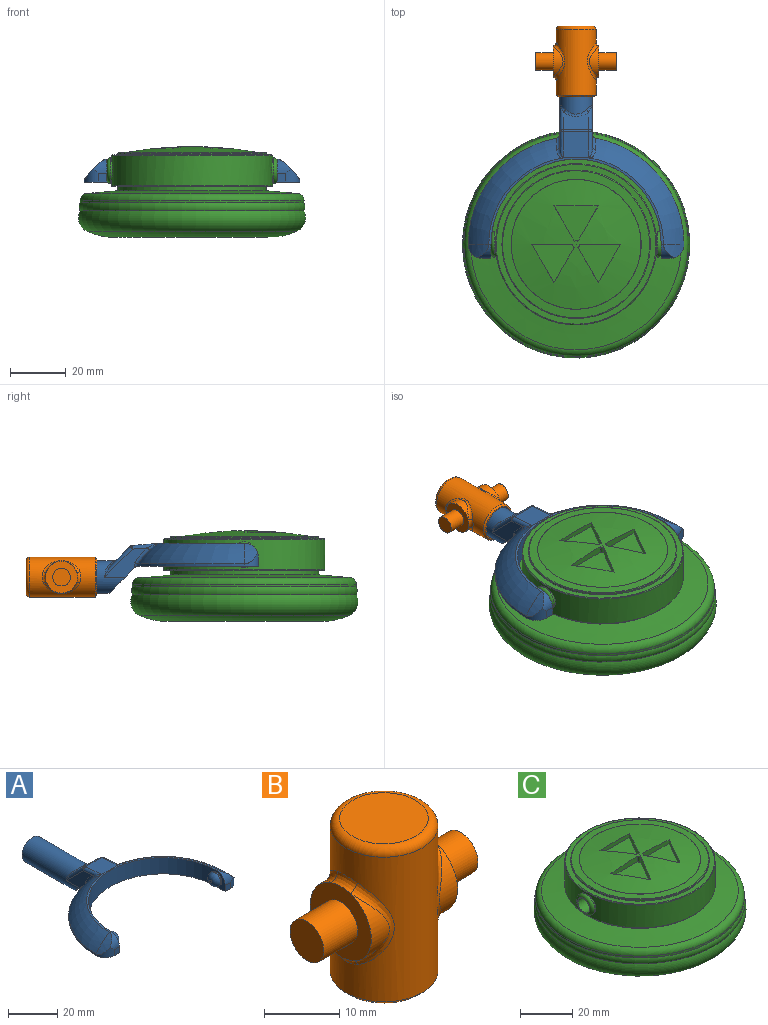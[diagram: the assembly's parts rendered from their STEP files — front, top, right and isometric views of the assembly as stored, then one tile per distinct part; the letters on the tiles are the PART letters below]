
ASSEMBLY  parts=3 mates=2
PART A: 48 faces, bbox 77.3x80.8x18.2 mm
  f0: plane 11.99x9.83mm, normal (0,-0.71,-0.71), area 141.5mm2, adj f1,f2,f9,f30,f43,f46
  f1: plane 15.39x10.49mm, normal (-1,0,0), area 63.5mm2, adj f0,f30,f32,f36,f46,f47
  f2: plane 15.39x10.49mm, normal (1,0,0), area 63.5mm2, adj f0,f30,f34,f39,f43,f44
  f3: plane 9.14x6.37mm, normal (0,0.71,0.71), area 67.6mm2, adj f35,f36,f39,f40
  f4: cylinder r=38.61mm len=37.99mm, axis (0,0,-1), area 42.6mm2, adj f6,f9,f17,f46,f47
  f5: torus R=19.3mm, axis (0,0,-1), area 507.8mm2, adj f10,f11,f12,f29,f42,f44
  f6: torus R=19.3mm, axis (0,0,-1), area 507.8mm2, adj f4,f11,f15,f28,f45,f47
  f7: cylinder r=30.48mm len=60.96mm, axis (0,0,-1), area 746.6mm2, adj f8,f9,f11,f14,f21,f24
  f8: plane 8.13x5.08mm, normal (-1,0,0), area 19.9mm2, adj f7,f9,f13,f19,f24
  f9: plane 77.22x43.73mm, normal (0,0,-1), area 956.2mm2, adj f0,f4,f7,f8,f10,f13,f14,f16
  f10: cylinder r=38.61mm len=37.99mm, axis (0,0,-1), area 42.6mm2, adj f5,f9,f20,f43,f44
  f11: plane 62.55x30.95mm, normal (0,0,1), area 75mm2, adj f5,f6,f7,f18,f19,f27
  f12: cylinder r=22.71mm len=7.33mm, axis (0,1,0), area 24.8mm2, adj f5,f19,f20
  f13: plane 3.05x3.05mm, normal (0,-1,0), area 9.3mm2, adj f8,f9,f19,f20
  f14: plane 8.13x5.08mm, normal (1,0,0), area 19.9mm2, adj f7,f9,f16,f18,f21
  f15: cylinder r=22.71mm len=7.33mm, axis (0,1,0), area 24.8mm2, adj f6,f17,f18
  f16: plane 3.05x3.05mm, normal (0,-1,0), area 9.3mm2, adj f9,f14,f17,f18
  f17: cylinder r=5.08mm len=5.08mm, axis (0,0,-1), area 21.9mm2, adj f4,f9,f15,f16,f18
  f18: cylinder r=5.08mm len=5.08mm, axis (-1,0,0), area 21.9mm2, adj f11,f14,f15,f16,f17
  f19: cylinder r=5.08mm len=5.08mm, axis (-1,0,0), area 21.9mm2, adj f8,f11,f12,f13,f20
  f20: cylinder r=5.08mm len=5.08mm, axis (0,0,-1), area 21.9mm2, adj f9,f10,f12,f13,f19
  f21: cylinder r=3.17mm len=6.35mm, axis (-1,0,0), area 12.7mm2, adj f7,f14,f23
  f22: plane 1.27x1.27mm, normal (1,0,0), area 1.3mm2, adj f23
  f23: torus R=0.64mm, axis (1,0,0), area 56.5mm2, adj f21,f22
  f24: cylinder r=3.17mm len=6.35mm, axis (1,0,0), area 12.7mm2, adj f7,f8,f26
  f25: plane 1.27x1.27mm, normal (-1,0,0), area 1.3mm2, adj f26
  f26: torus R=0.64mm, axis (-1,0,0), area 56.5mm2, adj f24,f25
  f27: plane 9.86x9.36mm, normal (0,0.09,1), area 85.6mm2, adj f11,f28,f29,f32,f34,f35,f42,f45
  f28: plane 1.04x0.17mm, normal (0,-1,0), area 0mm2, adj f6,f27,f45
  f29: plane 1.04x0.17mm, normal (0,-1,0), area 0mm2, adj f5,f27,f42
  f30: cylinder r=5.84mm len=33.01mm, axis (0,-1,0), area 1029.7mm2, adj f0,f1,f2,f31,f38,f40,f41
  f31: plane 11.68x11.68mm, normal (0,1,0), area 107.2mm2, adj f30
  f32: cylinder r=1.27mm len=9.13mm, axis (0,-1,0.09), area 14.4mm2, adj f1,f27,f33,f45
  f33: sphere r=1.27mm, area 1.5mm2, adj f32,f35,f36
  f34: cylinder r=1.27mm len=9.13mm, axis (0,1,-0.09), area 14.4mm2, adj f2,f27,f37,f42
  f35: cylinder r=1.27mm len=9.14mm, axis (-1,0,0), area 8.1mm2, adj f3,f27,f33,f37
  f36: cylinder r=1.27mm len=10.91mm, axis (0,-0.71,0.71), area 23.1mm2, adj f1,f3,f33,f38
  f37: sphere r=1.27mm, area 1.5mm2, adj f34,f35,f39
  f38: bspline ~4.55x2.75mm, area 2.3mm2, adj f30,f36,f40
  f39: cylinder r=1.27mm len=10.91mm, axis (0,0.71,-0.71), area 23.1mm2, adj f2,f3,f37,f41
  f40: bspline ~9.14x2.56mm, area 10.7mm2, adj f3,f30,f38,f41
  f41: bspline ~5.23x3.53mm, area 2.3mm2, adj f30,f39,f40
  f42: bspline ~4.62x3.14mm, area 5.2mm2, adj f5,f27,f29,f34,f44
  f43: cylinder r=1.27mm len=1.74mm, axis (0,0,-1), area 1.9mm2, adj f0,f2,f9,f10,f44
  f44: bspline ~8.6x7.86mm, area 11.9mm2, adj f2,f5,f10,f42,f43
  f45: bspline ~4.62x3.14mm, area 5.2mm2, adj f6,f27,f28,f32,f47
  f46: cylinder r=1.27mm len=1.74mm, axis (0,0,-1), area 1.9mm2, adj f0,f1,f4,f9,f47
  f47: bspline ~8.6x7.86mm, area 11.9mm2, adj f1,f4,f6,f45,f46
PART B: 25 faces, bbox 28.9x15.5x25.4 mm
  f0: cylinder r=5.71mm len=10.81mm, axis (-1,0,0), area 26.2mm2, adj f5,f15
  f1: cylinder r=5.71mm len=10.81mm, axis (-1,0,0), area 26.2mm2, adj f8,f11
  f2: cylinder r=7.14mm len=23.5mm, axis (0,0,-1), area 763.2mm2, adj f9,f10,f11,f12,f13,f14,f15,f16
  f3: plane 11.75x11.75mm, normal (0,0,1), area 108.4mm2, adj f17
  f4: plane 13.02x13.02mm, normal (0,0,-1), area 16.3mm2, adj f22,f24
  f5: plane 11.46x11.46mm, normal (1,0,0), area 70.9mm2, adj f0,f6,f13,f16,f18
  f6: cylinder r=5.71mm len=10.81mm, axis (-1,0,0), area 26.2mm2, adj f5,f14
  f7: cylinder r=5.71mm len=10.81mm, axis (-1,0,0), area 26.2mm2, adj f8,f10
  f8: plane 11.46x11.46mm, normal (-1,0,0), area 70.9mm2, adj f1,f7,f9,f12,f20
  f9: bspline ~4.64x1.73mm, area 6.5mm2, adj f2,f8,f10,f11
  f10: bspline ~13.62x4.91mm, area 20.7mm2, adj f2,f7,f9,f12
  f11: bspline ~13.6x4.87mm, area 20.7mm2, adj f1,f2,f9,f12
  f12: bspline ~4.64x1.73mm, area 6.5mm2, adj f2,f8,f10,f11
  f13: bspline ~4.64x1.73mm, area 6.5mm2, adj f2,f5,f14,f15
  f14: bspline ~13.62x4.91mm, area 20.7mm2, adj f2,f6,f13,f16
  f15: bspline ~13.6x4.87mm, area 20.7mm2, adj f0,f2,f13,f16
  f16: bspline ~4.64x1.73mm, area 6.5mm2, adj f2,f5,f14,f15
  f17: torus R=5.87mm, axis (0,0,1), area 83.8mm2, adj f2,f3
  f18: cylinder r=3.17mm len=6.35mm, axis (-1,0,0), area 126.7mm2, adj f5,f19
  f19: plane 6.35x6.35mm, normal (1,0,0), area 31.7mm2, adj f18
  f20: cylinder r=3.17mm len=6.35mm, axis (1,0,0), area 126.7mm2, adj f8,f21
  f21: plane 6.35x6.35mm, normal (-1,0,0), area 31.7mm2, adj f20
  f22: cylinder r=6.1mm len=22.86mm, axis (0,0,-1), area 875.6mm2, adj f4,f23
  f23: plane 12.19x12.19mm, normal (0,0,-1), area 116.7mm2, adj f22
  f24: cone r=7.14mm half-angle=45deg, axis (0,0,1), area 38.5mm2, adj f2,f4
PART C: 41 faces, bbox 96.3x96.3x32.5 mm
  f0: cylinder r=28.87mm len=57.73mm, axis (0,0,-1), area 1814.4mm2, adj f31,f32,f37,f38
  f1: sphere r=135.39mm, area 1385.3mm2, adj f15,f16,f17,f18,f20,f21,f22,f23
  f2: plane 39.35x39.35mm, normal (0,0,-1), area 1216.2mm2, adj f3
  f3: torus R=20.13mm, axis (0,0,-1), area 1430.4mm2, adj f2,f4
  f4: torus R=27.75mm, axis (0,0,-1), area 3543.7mm2, adj f3,f5
  f5: torus R=35.37mm, axis (0,0,-1), area 2180.8mm2, adj f4,f6
  f6: torus R=37.36mm, axis (0,0,-1), area 734.8mm2, adj f5,f7
  f7: cylinder r=40.07mm len=80.14mm, axis (0,0,-1), area 213.4mm2, adj f6,f14
  f8: cone r=26.58mm half-angle=85deg, axis (0,0,-1), area 2265.9mm2, adj f9,f14
  f9: cylinder r=26.58mm len=53.16mm, axis (0,0,-1), area 265.1mm2, adj f8,f10
  f10: plane 57.23x57.23mm, normal (0,0,-1), area 352.3mm2, adj f9,f37
  f11: plane 57.23x57.23mm, normal (0,0,1), area 352.3mm2, adj f12,f38
  f12: cylinder r=26.58mm len=53.16mm, axis (0,0,-1), area 92.3mm2, adj f11,f39
  f13: cone r=26.58mm half-angle=87deg, axis (0,0,-1), area 477.5mm2, adj f39,f40
  f14: torus R=37.53mm, axis (0,0,1), area 928.9mm2, adj f7,f8
  f15: cylinder r=1.27mm len=2.53mm, axis (0,0,1), area 3.4mm2, adj f1,f16,f18,f19
  f16: plane 12.65x7.3mm, normal (0.87,0.5,0), area 32.2mm2, adj f1,f15,f17,f19
  f17: plane 13.75x7.94mm, normal (-0.87,0.5,0), area 28mm2, adj f1,f16,f18,f19
  f18: plane 14.61x2.53mm, normal (0,-1,0), area 32.2mm2, adj f1,f15,f17,f19
  f19: plane 15.24x13.75mm, normal (0,0,1), area 108.3mm2, adj f15,f16,f17,f18
  f20: plane 15.88x1.84mm, normal (0,-1,0), area 28mm2, adj f1,f21,f23,f24
  f21: plane 12.65x7.3mm, normal (0.87,0.5,0), area 32.2mm2, adj f1,f20,f22,f24
  f22: cylinder r=1.27mm len=2.53mm, axis (0,0,1), area 3.4mm2, adj f1,f21,f23,f24
  f23: plane 12.65x7.3mm, normal (-0.87,0.5,0), area 32.2mm2, adj f1,f20,f22,f24
  f24: plane 15.88x12.65mm, normal (0,0,1), area 108.3mm2, adj f20,f21,f22,f23
  f25: cylinder r=1.27mm len=2.53mm, axis (0,0,1), area 3.4mm2, adj f1,f26,f28,f29
  f26: plane 14.61x2.53mm, normal (0,-1,0), area 32.2mm2, adj f1,f25,f27,f29
  f27: plane 13.75x7.94mm, normal (0.87,0.5,0), area 28mm2, adj f1,f26,f28,f29
  f28: plane 12.65x7.3mm, normal (-0.87,0.5,0), area 32.2mm2, adj f1,f25,f27,f29
  f29: plane 15.24x13.75mm, normal (0,0,1), area 108.3mm2, adj f25,f26,f27,f28
  f30: plane 6.6x6.6mm, normal (1,0,0), area 2.6mm2, adj f35,f36
  f31: cylinder r=4.57mm len=9.14mm, axis (-1,0,0), area 15.1mm2, adj f0,f35
  f32: cylinder r=4.57mm len=9.14mm, axis (-1,0,0), area 15.1mm2, adj f0,f34
  f33: plane 6.6x6.6mm, normal (-1,0,0), area 2.6mm2, adj f34,f36
  f34: torus R=3.3mm, axis (1,0,0), area 51.5mm2, adj f32,f33
  f35: torus R=3.3mm, axis (1,0,0), area 51.5mm2, adj f30,f31
  f36: cylinder r=3.17mm len=60.96mm, axis (1,0,0), area 1216.1mm2, adj f30,f33
  f37: torus R=28.61mm, axis (0,0,1), area 72.1mm2, adj f0,f10
  f38: torus R=28.61mm, axis (0,0,-1), area 72.1mm2, adj f0,f11
  f39: torus R=26.33mm, axis (0,0,1), area 64.2mm2, adj f12,f13
  f40: torus R=23.29mm, axis (0,0,1), area 4.5mm2, adj f1,f13
PLACE A t=(32.34,27.52,20.85)mm
PLACE B rot(axis=(-1,0,0),90deg) t=(32.34,80.3,16.88)mm
PLACE C t=(32.34,27.52,33.52)mm
MATE revolute A.f24 <-> C.f31  axis (-1,0,0) through (62.82,27.52,24.92)mm
MATE revolute B.f2 <-> A.f30  axis (0,-1,0) through (32.34,103.16,16.88)mm
